AUTODESK INVENTOR PART (.ipt)
format: ipt  version: 2018 (Build 220112000, 112)  size: 114,688 bytes
history: native  units: mm
features: sketch x1
ambient origin geometry x8: Origin, YZ Plane, XZ Plane, XY Plane, X Axis, Y Axis, Z Axis, Center Point
feature tree (1):
  sketch  "Sketch1"  dims[d1=48.5mm d3=120.0mm d4=40.0mm d5=40.0mm d6=130.0mm d7=35.0mm d8=35.0mm d9=2900.0mm d11=250.0mm d12=170.6mm d13=5.986479mm d14=80.0mm d15=250.0mm d16=80.0mm d17=170.6mm d18=240.0mm d19=5.986479mm]
